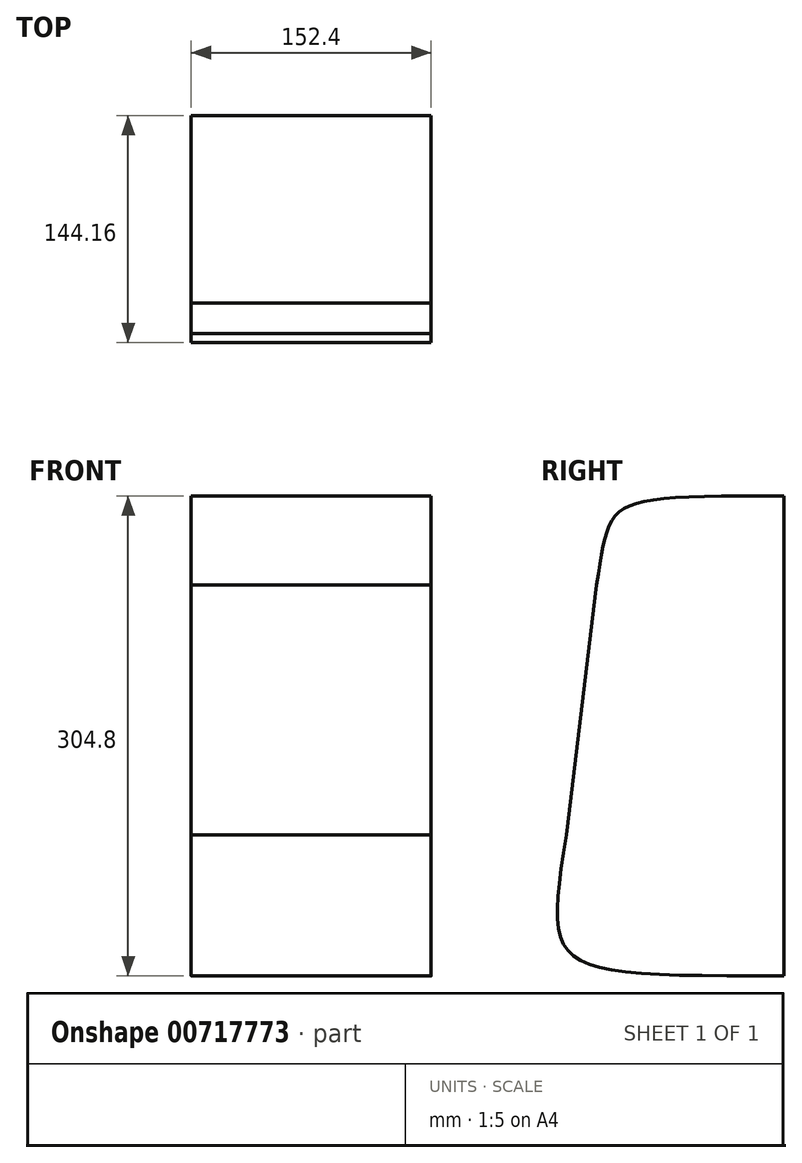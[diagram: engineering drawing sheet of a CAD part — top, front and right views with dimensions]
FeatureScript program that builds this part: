
annotation { "Feature Type Name" : "Feature", "Feature Type Description" : "" }
export const myFeature = defineFeature(function(context is Context, id is Id, definition is map)
    precondition{}
    {
        {
            var Q0;
            Q0=qCreatedBy(makeId("Front.planeOp"),FACE);
            var sketch = newSketch(context, id + "F0", { "sketchPlane" : qUnion([Q0])});
            skLineSegment(sketch, "E0.bottom", {"start": v(0, 0) * mm, "end": v(152.4, 0) * mm});
            skLineSegment(sketch, "E0.top", {"start": v(0, 304.8) * mm, "end": v(152.4, 304.8) * mm});
            skLineSegment(sketch, "E0.left", {"start": v(0, 0) * mm, "end": v(0, 304.8) * mm});
            skLineSegment(sketch, "E0.right", {"start": v(152.4, 0) * mm, "end": v(152.4, 304.8) * mm});
            skSolve(sketch);
        }
        {
            var Q0;
            Q0=qCreatedBy(makeId("Right.planeOp"),FACE);
            var sketch = newSketch(context, id + "F1", { "sketchPlane" : qUnion([Q0])});
            skLineSegment(sketch, "E1.bottom", {"start": v(0, 0) * mm, "end": v(-152.4, 0) * mm});
            skLineSegment(sketch, "E1.top", {"start": v(0, 304.8) * mm, "end": v(-152.4, 304.8) * mm});
            skLineSegment(sketch, "E1.left", {"start": v(0, 0) * mm, "end": v(0, 304.8) * mm});
            skLineSegment(sketch, "E1.right", {"start": v(-152.4, 0) * mm, "end": v(-152.4, 304.8) * mm});
            skLineSegment(sketch, "E2.left", {"start": v(-152.4, 179.22) * mm, "end": v(-152.4, 19.22) * mm});
            skFitSpline(sketch, "E3", {"points": [v(0, 304.8) * mm, v(-119.17, 248.28) * mm], "startDerivative": vector(-353.1, 0) * mm, "endDerivative": vector(-29.5, -169.57) * mm});
            skFitSpline(sketch, "E4", {"points": [v(-138.4, 89.44) * mm, v(0, 0) * mm], "startDerivative": vector(-42, -268.3) * mm, "endDerivative": vector(457.2, 0) * mm});
            skLineSegment(sketch, "E5", {"start": v(-138.4, 89.44) * mm, "end": v(-119.17, 248.28) * mm});
            skSolve(sketch);
        }
        {
            var Q0;
            Q0=makeQuery(id+"F1.imprint","IMPRINT",FACE,{"disambiguationData":[TD([[makeQuery(id+"F1.imprint","IMPRINT",EDGE,{"derivedFrom":sQuery(id+"F1.wireOp",EDGE,"E1.left")}),1.0]])]});
            extrude(context, id + "F2", {"entities" : qUnion([Q0]), "depth" : 152.4 * mm, "offsetDistance" : 25.4 * mm});
        }
    });
